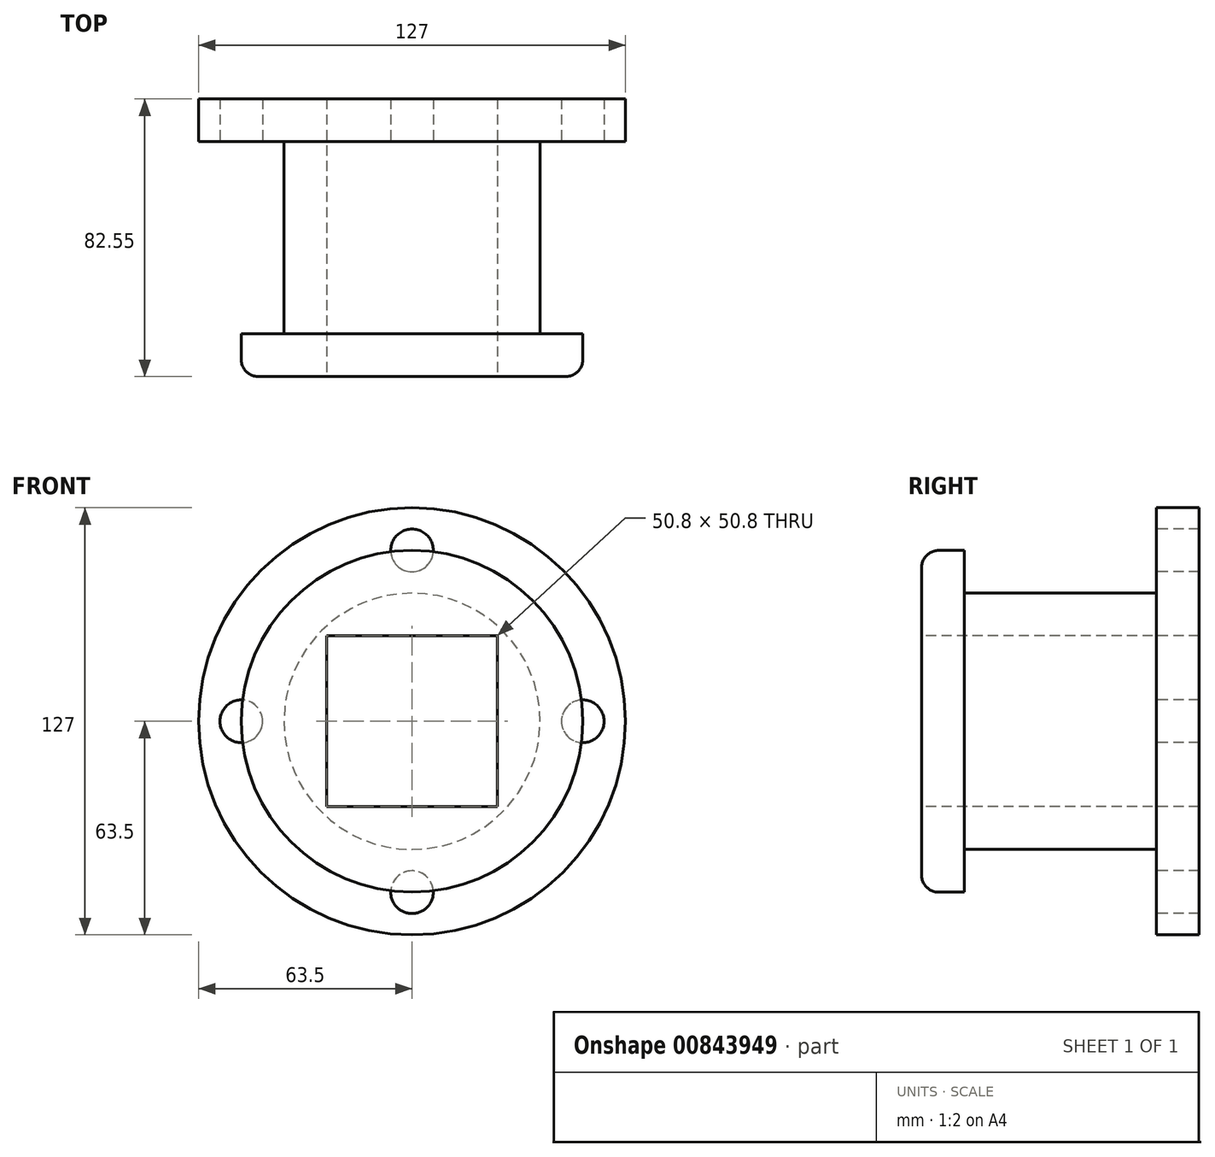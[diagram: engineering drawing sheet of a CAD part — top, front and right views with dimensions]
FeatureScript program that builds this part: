
annotation { "Feature Type Name" : "Feature", "Feature Type Description" : "" }
export const myFeature = defineFeature(function(context is Context, id is Id, definition is map)
    precondition{}
    {
        {
            var Q0;
            Q0=qCreatedBy(makeId("Front.planeOp"),FACE);
            var sketch = newSketch(context, id + "F0", { "sketchPlane" : qUnion([Q0])});
            skCircle(sketch, "E0", {"center": v(0, 0) * mm, "radius": 63.5 * mm});
            skSolve(sketch);
        }
        {
            var Q0;
            Q0=makeQuery(id+"F0.imprint","IMPRINT",FACE,{"disambiguationData":[TD([[makeQuery(id+"F0.imprint","IMPRINT",EDGE,{"derivedFrom":sQuery(id+"F0.wireOp",EDGE,"E0")}),1.0]])]});
            extrude(context, id + "F1", {"entities" : qUnion([Q0]), "depth" : 12.7 * mm, "offsetDistance" : 25.4 * mm});
        }
        {
            var Q0;
            Q0=makeQuery(id+"F1.opExtrude","CAP_FACE",FACE,{"disambiguationData":[OSD([sQuery(id+"F0.wireOp",EDGE,"E0")])],"isStart":false});
            var sketch = newSketch(context, id + "F2", { "sketchPlane" : qUnion([Q0])});
            skCircle(sketch, "E1", {"center": v(0, 0) * mm, "radius": 38.1 * mm});
            skSolve(sketch);
        }
        {
            var Q0;
            Q0=makeQuery(id+"F2.imprint","IMPRINT",FACE,{"disambiguationData":[TD([[makeQuery(id+"F2.imprint","IMPRINT",EDGE,{"derivedFrom":sQuery(id+"F2.wireOp",EDGE,"E1")}),1.0]])]});
            extrude(context, id + "F3", {"entities" : qUnion([Q0]), "operationType" : NewBodyOperationType.ADD, "depth" : 57.15 * mm, "offsetDistance" : 25.4 * mm});
        }
        {
            var Q0;
            Q0=makeQuery(id+"F3.opExtrude","CAP_FACE",FACE,{"disambiguationData":[OSD([sQuery(id+"F2.wireOp",EDGE,"E1")])],"isStart":false});
            var sketch = newSketch(context, id + "F4", { "sketchPlane" : qUnion([Q0])});
            skCircle(sketch, "E2", {"center": v(0, 0) * mm, "radius": 50.8 * mm});
            skSolve(sketch);
        }
        {
            var Q0;
            Q0 = qSketchRegion(id + "F4", true);
            extrude(context, id + "F5", {"entities" : qUnion([Q0]), "operationType" : NewBodyOperationType.ADD, "depth" : 12.7 * mm, "offsetDistance" : 25.4 * mm});
        }
        {
            var Q0;
            Q0=makeQuery(id+"F1.opExtrude","CAP_FACE",FACE,{"disambiguationData":[OSD([sQuery(id+"F0.wireOp",EDGE,"E0")])],"isStart":false});
            var sketch = newSketch(context, id + "F6", { "sketchPlane" : qUnion([Q0])});
            skCircle(sketch, "E3", {"center": v(50.8, 0) * mm, "radius": 6.35 * mm});
            skCircle(sketch, "E4.1.0", {"center": v(0, 50.8) * mm, "radius": 6.35 * mm});
            skCircle(sketch, "E4.2.0", {"center": v(-50.8, 0) * mm, "radius": 6.35 * mm});
            skCircle(sketch, "E4.3.0", {"center": v(0, -50.8) * mm, "radius": 6.35 * mm});
            skPoint(sketch, "E4.center", {"position": v(0, 0) * mm});
            skSolve(sketch);
        }
        {
            var Q0;
            Q0=makeQuery(id+"F6.imprint","IMPRINT",FACE,{"disambiguationData":[TD([[makeQuery(id+"F6.imprint","IMPRINT",EDGE,{"derivedFrom":sQuery(id+"F6.wireOp",EDGE,"E3")}),1.0]])]});
            var Q1;
            Q1=makeQuery(id+"F6.imprint","IMPRINT",FACE,{"disambiguationData":[TD([[makeQuery(id+"F6.imprint","IMPRINT",EDGE,{"derivedFrom":sQuery(id+"F6.wireOp",EDGE,"E4.1.0")}),1.0]])]});
            var Q2;
            Q2=makeQuery(id+"F6.imprint","IMPRINT",FACE,{"disambiguationData":[TD([[makeQuery(id+"F6.imprint","IMPRINT",EDGE,{"derivedFrom":sQuery(id+"F6.wireOp",EDGE,"E4.2.0")}),1.0]])]});
            var Q3;
            Q3=makeQuery(id+"F6.imprint","IMPRINT",FACE,{"disambiguationData":[TD([[makeQuery(id+"F6.imprint","IMPRINT",EDGE,{"derivedFrom":sQuery(id+"F6.wireOp",EDGE,"E4.3.0")}),1.0]])]});
            extrude(context, id + "F7", {"entities" : qUnion([Q0, Q1, Q2, Q3]), "operationType" : NewBodyOperationType.REMOVE, "oppositeDirection" : true, "depth" : 25.4 * mm, "offsetDistance" : 25.4 * mm});
        }
        {
            var Q0;
            Q0=makeQuery(id+"F5.opExtrude","CAP_FACE",FACE,{"disambiguationData":[OSD([sQuery(id+"F4.wireOp",EDGE,"E2")])],"isStart":false});
            var sketch = newSketch(context, id + "F8", { "sketchPlane" : qUnion([Q0])});
            skLineSegment(sketch, "E5.bottom", {"start": v(25.4, 25.4) * mm, "end": v(-25.4, 25.4) * mm});
            skLineSegment(sketch, "E5.top", {"start": v(25.4, -25.4) * mm, "end": v(-25.4, -25.4) * mm});
            skLineSegment(sketch, "E5.left", {"start": v(25.4, 25.4) * mm, "end": v(25.4, -25.4) * mm});
            skLineSegment(sketch, "E5.right", {"start": v(-25.4, 25.4) * mm, "end": v(-25.4, -25.4) * mm});
            skPoint(sketch, "E5.middle", {"position": v(0, 0) * mm});
            skSolve(sketch);
        }
        {
            var Q0;
            Q0 = qSketchRegion(id + "F8", true);
            extrude(context, id + "F9", {"entities" : qUnion([Q0]), "operationType" : NewBodyOperationType.REMOVE, "oppositeDirection" : true, "depth" : 127 * mm, "offsetDistance" : 25.4 * mm});
        }
        {
            var Q0;
            Q0=makeQuery(id+"F5.opExtrude","CAP_EDGE",EDGE,{"disambiguationData":[OSD([sQuery(id+"F4.wireOp",EDGE,"E2")])],"isStart":false});
            fillet(context, id + "F10", {"entities" : qUnion([Q0]), "radius" : 5.08 * mm, "tangentPropagation" : true, "allowEdgeOverflow" : false});
        }
    });
